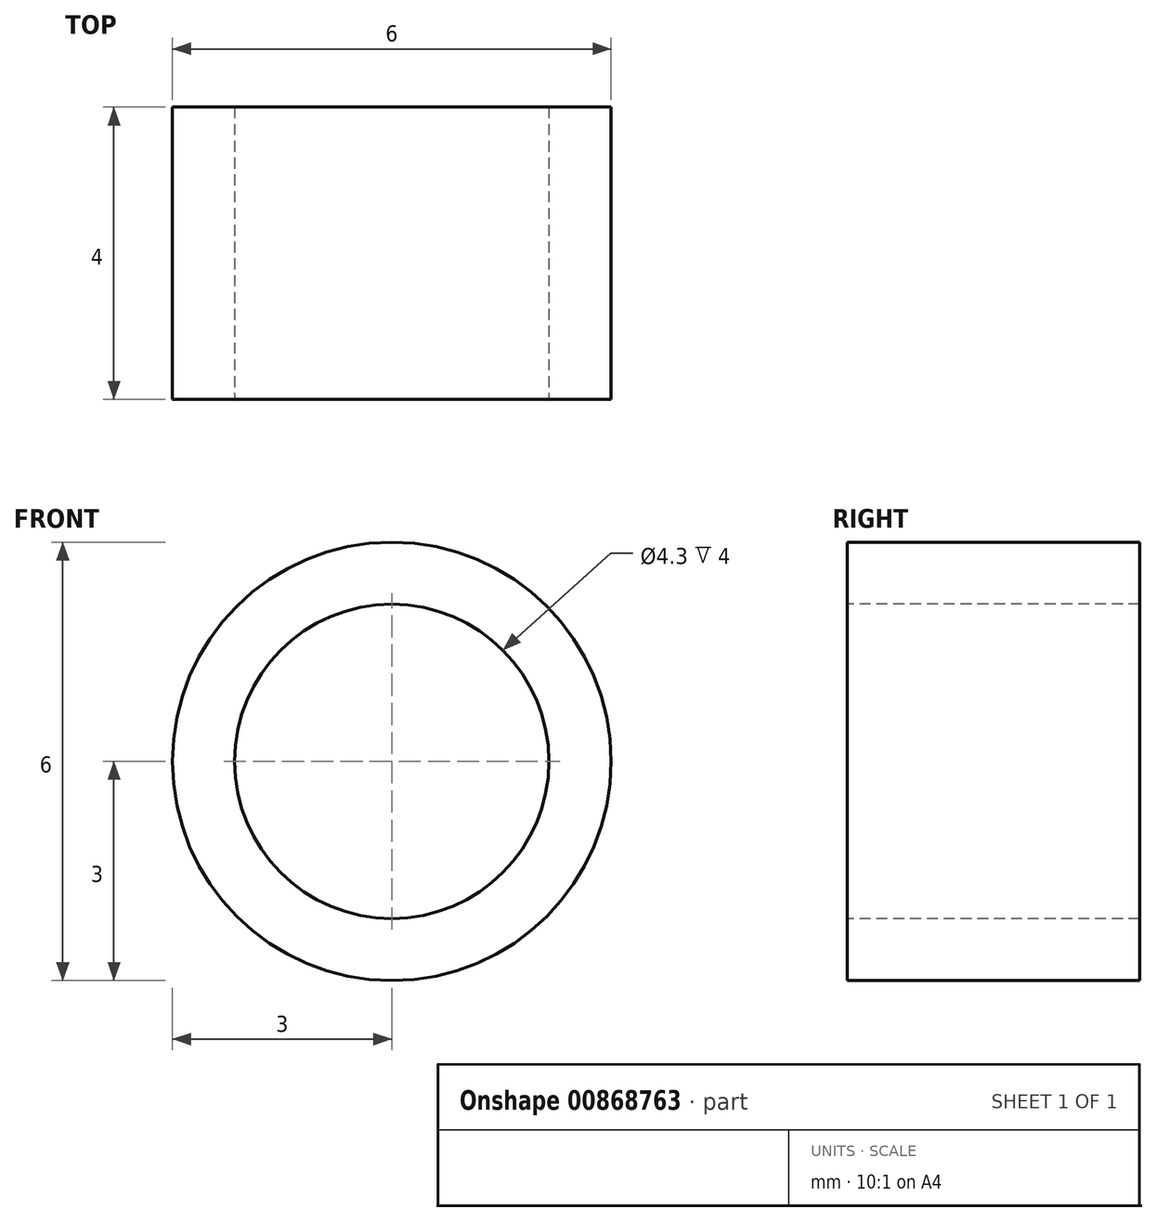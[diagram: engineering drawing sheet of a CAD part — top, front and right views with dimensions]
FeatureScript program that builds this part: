
annotation { "Feature Type Name" : "Feature", "Feature Type Description" : "" }
export const myFeature = defineFeature(function(context is Context, id is Id, definition is map)
    precondition{}
    {
        {
            var Q0;
            Q0=qCreatedBy(makeId("Front.planeOp"),FACE);
            var sketch = newSketch(context, id + "F0", { "sketchPlane" : qUnion([Q0])});
            skCircle(sketch, "E0", {"center": v(0, 0) * mm, "radius": 3 * mm});
            skCircle(sketch, "E1", {"center": v(0, 0) * mm, "radius": 2.15 * mm});
            skSolve(sketch);
        }
        {
            var Q0;
            Q0=makeQuery(id+"F0.imprint","IMPRINT",FACE,{"disambiguationData":[TD([[makeQuery(id+"F0.imprint","IMPRINT",EDGE,{"derivedFrom":sQuery(id+"F0.wireOp",EDGE,"E0")}),1.0]])]});
            extrude(context, id + "F1", {"entities" : qUnion([Q0]), "oppositeDirection" : true, "depth" : 4 * mm, "offsetDistance" : 25 * mm});
        }
    });
